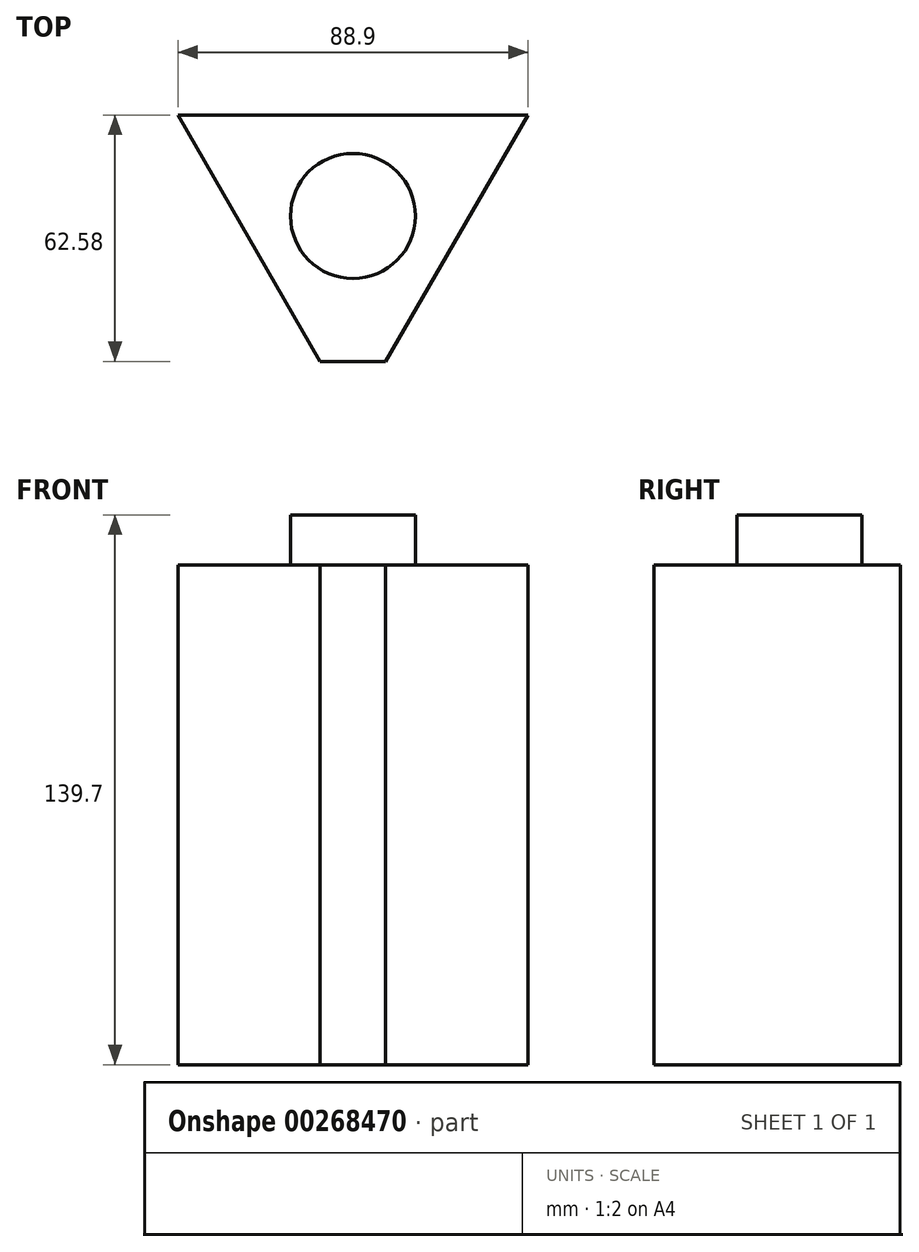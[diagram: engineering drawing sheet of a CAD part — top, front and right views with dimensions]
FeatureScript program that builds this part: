
annotation { "Feature Type Name" : "Feature", "Feature Type Description" : "" }
export const myFeature = defineFeature(function(context is Context, id is Id, definition is map)
    precondition{}
    {
        {
            var Q0;
            Q0=qCreatedBy(makeId("Top.planeOp"),FACE);
            var sketch = newSketch(context, id + "F0", { "sketchPlane" : qUnion([Q0])});
            skCircle(sketch, "E0.cCircle", {"center": v(0, 0) * mm, "radius": 25.66 * mm, "construction": true});
            skLineSegment(sketch, "E0.0", {"start": v(-44.45, 25.66) * mm, "end": v(44.45, 25.66) * mm});
            skLineSegment(sketch, "E0.1", {"start": v(44.45, 25.66) * mm, "end": v(0, -51.33) * mm});
            skLineSegment(sketch, "E0.2", {"start": v(0, -51.33) * mm, "end": v(-44.45, 25.66) * mm});
            skPoint(sketch, "E0.0.midPoint", {"position": v(0, 25.66) * mm});
            skSolve(sketch);
        }
        {
            var Q0;
            Q0=qSketchRegion(id+"F0",true);
            extrude(context, id + "F1", {"entities" : qUnion([Q0]), "depth" : 127 * mm});
        }
        {
            var Q0;
            Q0=qCreatedBy(makeId("Top.planeOp"),FACE);
            var sketch = newSketch(context, id + "F2", { "sketchPlane" : qUnion([Q0])});
            skLineSegment(sketch, "E1.bottom", {"start": v(-45.03, 26.58) * mm, "end": v(44.53, 26.58) * mm});
            skLineSegment(sketch, "E1.top", {"start": v(-45.03, -36.92) * mm, "end": v(44.53, -36.92) * mm});
            skLineSegment(sketch, "E1.left", {"start": v(-45.03, 26.58) * mm, "end": v(-45.03, -36.92) * mm});
            skLineSegment(sketch, "E1.right", {"start": v(44.53, 26.58) * mm, "end": v(44.53, -36.92) * mm});
            skSolve(sketch);
        }
        {
            var Q0;
            Q0=qSketchRegion(id+"F2",true);
            extrude(context, id + "F3", {"entities" : qUnion([Q0]), "operationType" : NewBodyOperationType.INTERSECT, "depth" : 215.9 * mm});
        }
        {
            var Q0;
            Q0=qCreatedBy(makeId("Top.planeOp"),FACE);
            var sketch = newSketch(context, id + "F4", { "sketchPlane" : qUnion([Q0])});
            skCircle(sketch, "E2", {"center": v(0, 0) * mm, "radius": 15.88 * mm});
            skSolve(sketch);
        }
        {
            var Q0;
            Q0=qSketchRegion(id+"F4",true);
            extrude(context, id + "F5", {"entities" : qUnion([Q0]), "operationType" : NewBodyOperationType.ADD, "depth" : 139.7 * mm});
        }
    });
